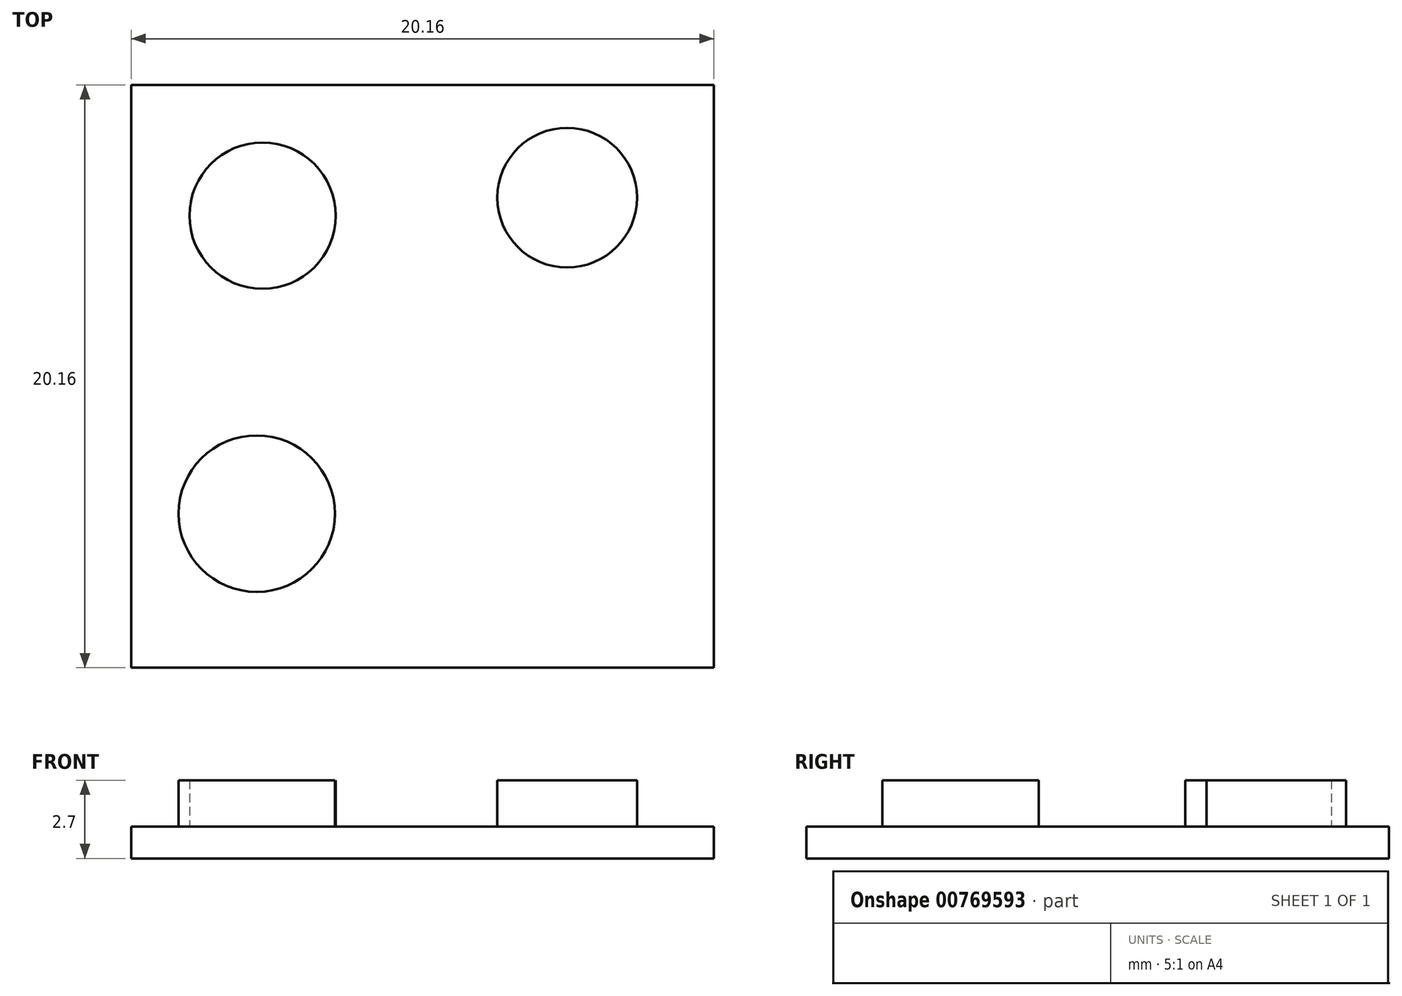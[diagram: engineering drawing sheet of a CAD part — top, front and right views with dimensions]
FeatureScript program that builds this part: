
annotation { "Feature Type Name" : "Feature", "Feature Type Description" : "" }
export const myFeature = defineFeature(function(context is Context, id is Id, definition is map)
    precondition{}
    {
        {
            var Q0;
            Q0=qCreatedBy(makeId("Top.planeOp"),FACE);
            var sketch = newSketch(context, id + "F0", { "sketchPlane" : qUnion([Q0])});
            skLineSegment(sketch, "E0.bottom", {"start": v(-13.38, 10.47) * mm, "end": v(6.78, 10.47) * mm});
            skLineSegment(sketch, "E0.top", {"start": v(-13.38, -9.7) * mm, "end": v(6.78, -9.7) * mm});
            skLineSegment(sketch, "E0.left", {"start": v(-13.38, 10.47) * mm, "end": v(-13.38, -9.7) * mm});
            skLineSegment(sketch, "E0.right", {"start": v(6.78, 10.47) * mm, "end": v(6.78, -9.7) * mm});
            skSolve(sketch);
        }
        {
            var Q0;
            Q0=makeQuery(id+"F0.imprint","IMPRINT",FACE,{"disambiguationData":[TD([[makeQuery(id+"F0.imprint","IMPRINT",EDGE,{"derivedFrom":sQuery(id+"F0.wireOp",EDGE,"E0.bottom")}),-1.0]])]});
            extrude(context, id + "F1", {"entities" : qUnion([Q0]), "depth" : 1.1 * mm, "offsetDistance" : 25 * mm});
        }
        {
            var Q0;
            Q0=makeQuery(id+"F1.opExtrude","CAP_FACE",FACE,{"disambiguationData":[OSD([sQuery(id+"F0.wireOp",EDGE,"E0.bottom"),sQuery(id+"F0.wireOp",EDGE,"E0.top"),sQuery(id+"F0.wireOp",EDGE,"E0.left"),sQuery(id+"F0.wireOp",EDGE,"E0.right")])],"isStart":false});
            var sketch = newSketch(context, id + "F2", { "sketchPlane" : qUnion([Q0])});
            skCircle(sketch, "E1", {"center": v(-8.84, 5.94) * mm, "radius": 2.53 * mm});
            skCircle(sketch, "E2", {"center": v(1.7, 6.57) * mm, "radius": 2.42 * mm});
            skCircle(sketch, "E3", {"center": v(-9.04, -4.36) * mm, "radius": 2.7 * mm});
            skSolve(sketch);
        }
        {
            var Q0;
            Q0=makeQuery(id+"F2.imprint","IMPRINT",FACE,{"disambiguationData":[TD([[makeQuery(id+"F2.imprint","IMPRINT",EDGE,{"derivedFrom":sQuery(id+"F2.wireOp",EDGE,"E1")}),1.0]])]});
            var Q1;
            Q1=makeQuery(id+"F2.imprint","IMPRINT",FACE,{"disambiguationData":[TD([[makeQuery(id+"F2.imprint","IMPRINT",EDGE,{"derivedFrom":sQuery(id+"F2.wireOp",EDGE,"E2")}),1.0]])]});
            var Q2;
            Q2=makeQuery(id+"F2.imprint","IMPRINT",FACE,{"disambiguationData":[TD([[makeQuery(id+"F2.imprint","IMPRINT",EDGE,{"derivedFrom":sQuery(id+"F2.wireOp",EDGE,"E3")}),1.0]])]});
            extrude(context, id + "F3", {"entities" : qUnion([Q0, Q1, Q2]), "operationType" : NewBodyOperationType.ADD, "depth" : 1.6 * mm, "offsetDistance" : 25 * mm});
        }
    });
